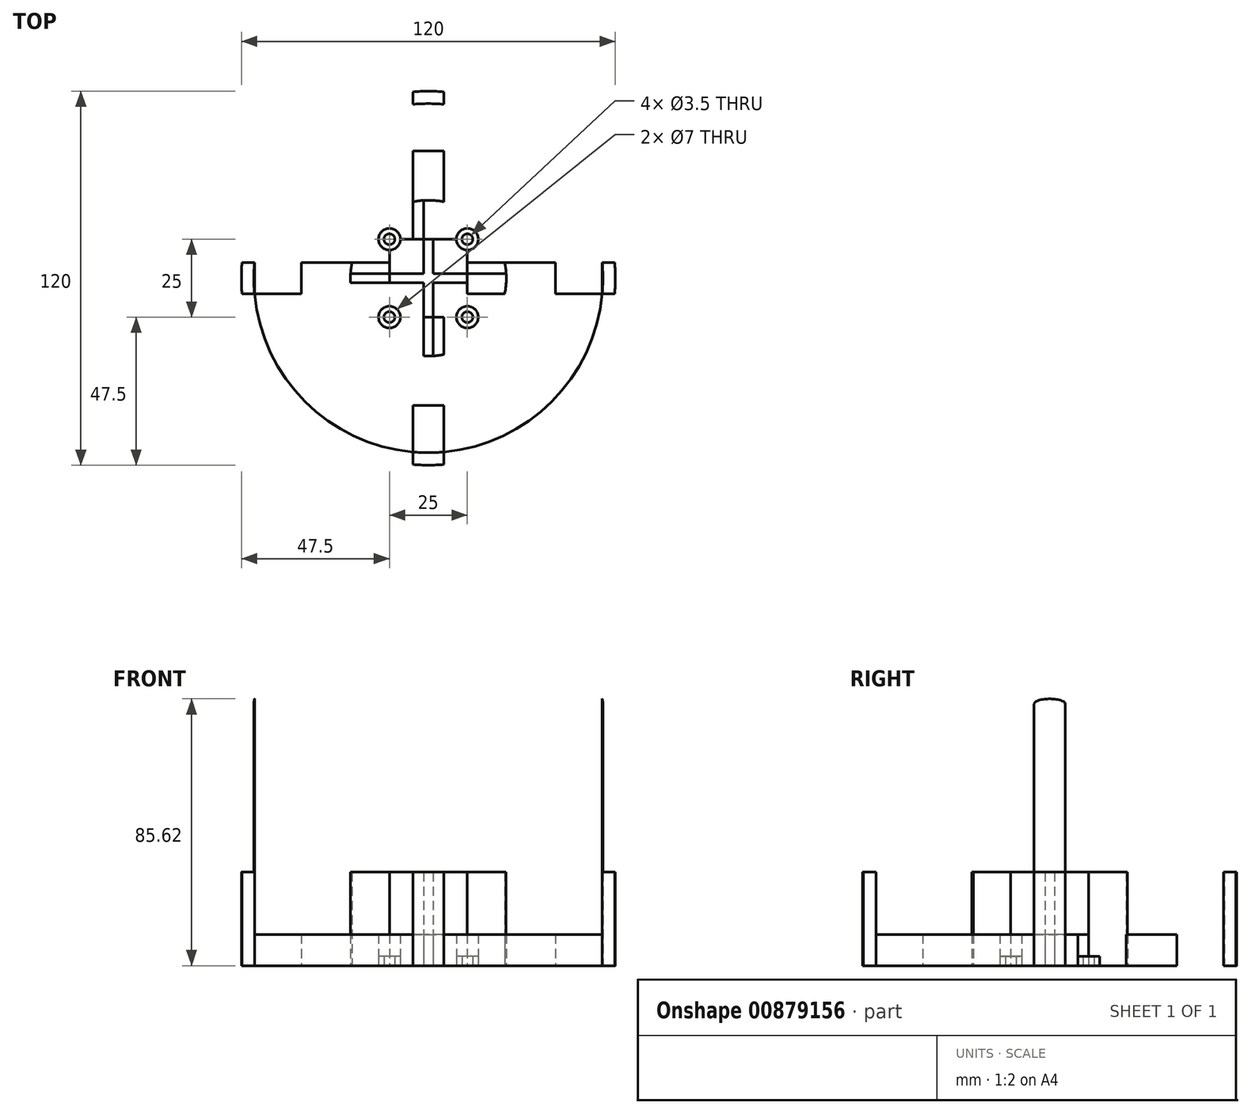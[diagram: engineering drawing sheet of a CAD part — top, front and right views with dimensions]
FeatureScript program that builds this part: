
annotation { "Feature Type Name" : "Feature", "Feature Type Description" : "" }
export const myFeature = defineFeature(function(context is Context, id is Id, definition is map)
    precondition{}
    {
        {
            var Q0;
            Q0=qCreatedBy(makeId("Top.planeOp"),FACE);
            var sketch = newSketch(context, id + "F0", { "sketchPlane" : qUnion([Q0])});
            skCircle(sketch, "E0", {"center": v(0, 0) * mm, "radius": 60 * mm});
            skCircle(sketch, "E1", {"center": v(0, 0) * mm, "radius": 56 * mm});
            skLineSegment(sketch, "E2.bottom", {"start": v(5, 55.78) * mm, "end": v(-5, 55.78) * mm});
            skLineSegment(sketch, "E2.top", {"start": v(5, -55.78) * mm, "end": v(-5, -55.78) * mm});
            skLineSegment(sketch, "E2.left", {"start": v(5, 55.78) * mm, "end": v(5, -55.78) * mm});
            skLineSegment(sketch, "E2.right", {"start": v(-5, 55.78) * mm, "end": v(-5, -55.78) * mm});
            skLineSegment(sketch, "E3.bottom", {"start": v(55.78, -5) * mm, "end": v(-55.78, -5) * mm});
            skLineSegment(sketch, "E3.top", {"start": v(55.78, 5) * mm, "end": v(-55.78, 5) * mm});
            skLineSegment(sketch, "E3.left", {"start": v(55.78, -5) * mm, "end": v(55.78, 5) * mm});
            skLineSegment(sketch, "E3.right", {"start": v(-55.78, -5) * mm, "end": v(-55.78, 5) * mm});
            skLineSegment(sketch, "E4.bottom", {"start": v(-5, 55.78) * mm, "end": v(5, 55.78) * mm});
            skLineSegment(sketch, "E4.top", {"start": v(-5, 40.78) * mm, "end": v(5, 40.78) * mm});
            skLineSegment(sketch, "E4.left", {"start": v(-5, 55.78) * mm, "end": v(-5, 40.78) * mm});
            skLineSegment(sketch, "E4.right", {"start": v(5, 55.78) * mm, "end": v(5, 40.78) * mm});
            skLineSegment(sketch, "E5.bottom", {"start": v(-55.78, -5) * mm, "end": v(-40.78, -5) * mm});
            skLineSegment(sketch, "E5.top", {"start": v(-55.78, 5) * mm, "end": v(-40.78, 5) * mm});
            skLineSegment(sketch, "E5.right", {"start": v(-40.78, -5) * mm, "end": v(-40.78, 5) * mm});
            skLineSegment(sketch, "E6.bottom", {"start": v(-5, -55.78) * mm, "end": v(5, -55.78) * mm});
            skLineSegment(sketch, "E6.top", {"start": v(-5, -40.78) * mm, "end": v(5, -40.78) * mm});
            skLineSegment(sketch, "E6.left", {"start": v(-5, -55.78) * mm, "end": v(-5, -40.78) * mm});
            skLineSegment(sketch, "E6.right", {"start": v(5, -55.78) * mm, "end": v(5, -40.78) * mm});
            skLineSegment(sketch, "E7.bottom", {"start": v(55.78, -5) * mm, "end": v(40.78, -5) * mm});
            skLineSegment(sketch, "E7.top", {"start": v(55.78, 5) * mm, "end": v(40.78, 5) * mm});
            skLineSegment(sketch, "E7.right", {"start": v(40.78, -5) * mm, "end": v(40.78, 5) * mm});
            skCircle(sketch, "E8", {"center": v(0, 0) * mm, "radius": 25 * mm});
            skLineSegment(sketch, "E9", {"start": v(-55.78, 5) * mm, "end": v(-59.8, 5) * mm});
            skLineSegment(sketch, "E10", {"start": v(-55.78, -5) * mm, "end": v(-59.8, -5) * mm});
            skLineSegment(sketch, "E11", {"start": v(-5, 55.78) * mm, "end": v(-5, 59.8) * mm});
            skLineSegment(sketch, "E12", {"start": v(5, 55.78) * mm, "end": v(5, 59.8) * mm});
            skLineSegment(sketch, "E13", {"start": v(55.78, 5) * mm, "end": v(59.8, 5) * mm});
            skLineSegment(sketch, "E14", {"start": v(55.78, -5) * mm, "end": v(59.8, -5) * mm});
            skLineSegment(sketch, "E15", {"start": v(-5, -55.78) * mm, "end": v(-5, -59.8) * mm});
            skLineSegment(sketch, "E16", {"start": v(5, -55.78) * mm, "end": v(5, -59.8) * mm});
            skLineSegment(sketch, "E17.bottom", {"start": v(12.5, 12.5) * mm, "end": v(-12.5, 12.5) * mm});
            skLineSegment(sketch, "E17.top", {"start": v(12.5, -12.5) * mm, "end": v(-12.5, -12.5) * mm});
            skLineSegment(sketch, "E17.left", {"start": v(12.5, 12.5) * mm, "end": v(12.5, -12.5) * mm});
            skLineSegment(sketch, "E17.right", {"start": v(-12.5, 12.5) * mm, "end": v(-12.5, -12.5) * mm});
            skCircle(sketch, "E18", {"center": v(-12.5, 12.5) * mm, "radius": 3.5 * mm});
            skCircle(sketch, "E19", {"center": v(-12.5, 12.5) * mm, "radius": 1.75 * mm});
            skCircle(sketch, "E20", {"center": v(12.5, 12.5) * mm, "radius": 3.5 * mm});
            skCircle(sketch, "E21", {"center": v(12.5, 12.5) * mm, "radius": 1.75 * mm});
            skCircle(sketch, "E22", {"center": v(-12.5, -12.5) * mm, "radius": 3.5 * mm});
            skCircle(sketch, "E23", {"center": v(-12.5, -12.5) * mm, "radius": 1.75 * mm});
            skCircle(sketch, "E24", {"center": v(12.5, -12.5) * mm, "radius": 3.5 * mm});
            skCircle(sketch, "E25", {"center": v(12.5, -12.5) * mm, "radius": 1.75 * mm});
            skLineSegment(sketch, "E26.bottom", {"start": v(40.78, 1.5) * mm, "end": v(-40.78, 1.5) * mm});
            skLineSegment(sketch, "E26.top", {"start": v(40.78, -1.5) * mm, "end": v(-40.78, -1.5) * mm});
            skLineSegment(sketch, "E26.left", {"start": v(40.78, 1.5) * mm, "end": v(40.78, -1.5) * mm});
            skLineSegment(sketch, "E26.right", {"start": v(-40.78, 1.5) * mm, "end": v(-40.78, -1.5) * mm});
            skLineSegment(sketch, "E27.bottom", {"start": v(1.5, 40.78) * mm, "end": v(-1.5, 40.78) * mm});
            skLineSegment(sketch, "E27.top", {"start": v(1.5, -40.78) * mm, "end": v(-1.5, -40.78) * mm});
            skLineSegment(sketch, "E27.left", {"start": v(1.5, 40.78) * mm, "end": v(1.5, -40.78) * mm});
            skLineSegment(sketch, "E27.right", {"start": v(-1.5, 40.78) * mm, "end": v(-1.5, -40.78) * mm});
            skSolve(sketch);
        }
        {
            var Q0;
            {var subQ0=sQuery(id+"F0.wireOp",EDGE,"E8");var subQ1=sQuery(id+"F0.wireOp",EDGE,"E2.left");var subQ2=makeQuery(id+"F0.imprint","INTERSECT",VERTEX,{"disambiguationData":[OD(0.0)],"derivedFrom":[subQ1,subQ0]});Q0=makeQuery(id+"F0.imprint","IMPRINT",FACE,{"disambiguationData":[TD([[makeQuery(id+"F0.imprint","IMPRINT",EDGE,{"disambiguationData":[TD([[subQ2,-1.0]])],"derivedFrom":subQ1}),1.0]])]});}
            var Q1;
            {var subQ0=sQuery(id+"F0.wireOp",EDGE,"E8");var subQ1=sQuery(id+"F0.wireOp",EDGE,"E2.left");var subQ2=makeQuery(id+"F0.imprint","INTERSECT",VERTEX,{"disambiguationData":[OD(0.0)],"derivedFrom":[subQ1,subQ0]});Q1=makeQuery(id+"F0.imprint","IMPRINT",FACE,{"disambiguationData":[TD([[makeQuery(id+"F0.imprint","IMPRINT",EDGE,{"disambiguationData":[TD([[subQ2,-1.0]])],"derivedFrom":subQ1}),-1.0]])]});}
            var Q2;
            {var subQ1=sQuery(id+"F0.wireOp",EDGE,"E2.right");var subQ5=sQuery(id+"F0.wireOp",EDGE,"E8");var subQ6=makeQuery(id+"F0.imprint","INTERSECT",VERTEX,{"disambiguationData":[OD(0.0)],"derivedFrom":[subQ1,subQ5]});Q2=makeQuery(id+"F0.imprint","IMPRINT",FACE,{"disambiguationData":[TD([[makeQuery(id+"F0.imprint","IMPRINT",EDGE,{"disambiguationData":[TD([[subQ6,-1.0]])],"derivedFrom":subQ1}),-1.0]])]});}
            var Q3;
            {var subQ5=sQuery(id+"F0.wireOp",EDGE,"E2.right");var subQ7=sQuery(id+"F0.wireOp",EDGE,"E17.bottom");var subQ8=makeQuery(id+"F0.imprint","INTERSECT",VERTEX,{"derivedFrom":[subQ5,subQ7]});Q3=makeQuery(id+"F0.imprint","IMPRINT",FACE,{"disambiguationData":[TD([[makeQuery(id+"F0.imprint","IMPRINT",EDGE,{"disambiguationData":[TD([[subQ8,-1.0]])],"derivedFrom":subQ5}),-1.0]])]});}
            var Q4;
            {var subQ0=sQuery(id+"F0.wireOp",EDGE,"E17.bottom");var subQ1=sQuery(id+"F0.wireOp",EDGE,"E2.left");var subQ2=makeQuery(id+"F0.imprint","INTERSECT",VERTEX,{"derivedFrom":[subQ1,subQ0]});Q4=makeQuery(id+"F0.imprint","IMPRINT",FACE,{"disambiguationData":[TD([[makeQuery(id+"F0.imprint","IMPRINT",EDGE,{"disambiguationData":[TD([[subQ2,-1.0]])],"derivedFrom":subQ1}),-1.0]])]});}
            var Q5;
            {var subQ5=sQuery(id+"F0.wireOp",EDGE,"E2.left");var subQ7=sQuery(id+"F0.wireOp",EDGE,"E17.bottom");var subQ8=makeQuery(id+"F0.imprint","INTERSECT",VERTEX,{"derivedFrom":[subQ5,subQ7]});Q5=makeQuery(id+"F0.imprint","IMPRINT",FACE,{"disambiguationData":[TD([[makeQuery(id+"F0.imprint","IMPRINT",EDGE,{"disambiguationData":[TD([[subQ8,-1.0]])],"derivedFrom":subQ5}),1.0]])]});}
            var Q6;
            {var subQ0=sQuery(id+"F0.wireOp",EDGE,"E3.top");var subQ1=sQuery(id+"F0.wireOp",EDGE,"E2.left");var subQ2=makeQuery(id+"F0.imprint","INTERSECT",VERTEX,{"derivedFrom":[subQ1,subQ0]});Q6=makeQuery(id+"F0.imprint","IMPRINT",FACE,{"disambiguationData":[TD([[makeQuery(id+"F0.imprint","IMPRINT",EDGE,{"disambiguationData":[TD([[subQ2,-1.0]])],"derivedFrom":subQ1}),1.0]])]});}
            var Q7;
            {var subQ0=sQuery(id+"F0.wireOp",EDGE,"E3.top");var subQ1=sQuery(id+"F0.wireOp",EDGE,"E2.left");var subQ2=makeQuery(id+"F0.imprint","INTERSECT",VERTEX,{"derivedFrom":[subQ1,subQ0]});Q7=makeQuery(id+"F0.imprint","IMPRINT",FACE,{"disambiguationData":[TD([[makeQuery(id+"F0.imprint","IMPRINT",EDGE,{"disambiguationData":[TD([[subQ2,-1.0]])],"derivedFrom":subQ1}),-1.0]])]});}
            var Q8;
            {var subQ0=sQuery(id+"F0.wireOp",EDGE,"E3.top");var subQ1=sQuery(id+"F0.wireOp",EDGE,"E2.right");var subQ2=makeQuery(id+"F0.imprint","INTERSECT",VERTEX,{"derivedFrom":[subQ1,subQ0]});Q8=makeQuery(id+"F0.imprint","IMPRINT",FACE,{"disambiguationData":[TD([[makeQuery(id+"F0.imprint","IMPRINT",EDGE,{"disambiguationData":[TD([[subQ2,-1.0]])],"derivedFrom":subQ1}),-1.0]])]});}
            var Q9;
            {var subQ0=sQuery(id+"F0.wireOp",EDGE,"E17.right");var subQ1=sQuery(id+"F0.wireOp",EDGE,"E3.bottom");var subQ2=makeQuery(id+"F0.imprint","INTERSECT",VERTEX,{"derivedFrom":[subQ1,subQ0]});Q9=makeQuery(id+"F0.imprint","IMPRINT",FACE,{"disambiguationData":[TD([[makeQuery(id+"F0.imprint","IMPRINT",EDGE,{"disambiguationData":[TD([[subQ2,-1.0]])],"derivedFrom":subQ1}),-1.0]])]});}
            var Q10;
            {var subQ0=sQuery(id+"F0.wireOp",EDGE,"E17.top");var subQ1=sQuery(id+"F0.wireOp",EDGE,"E2.right");var subQ2=makeQuery(id+"F0.imprint","INTERSECT",VERTEX,{"derivedFrom":[subQ1,subQ0]});Q10=makeQuery(id+"F0.imprint","IMPRINT",FACE,{"disambiguationData":[TD([[makeQuery(id+"F0.imprint","IMPRINT",EDGE,{"disambiguationData":[TD([[subQ2,-1.0]])],"derivedFrom":subQ1}),-1.0]])]});}
            var Q11;
            {var subQ1=sQuery(id+"F0.wireOp",EDGE,"E3.bottom");var subQ7=sQuery(id+"F0.wireOp",EDGE,"E2.right");var subQ8=makeQuery(id+"F0.imprint","INTERSECT",VERTEX,{"derivedFrom":[subQ7,subQ1]});Q11=makeQuery(id+"F0.imprint","IMPRINT",FACE,{"disambiguationData":[TD([[makeQuery(id+"F0.imprint","IMPRINT",EDGE,{"disambiguationData":[TD([[subQ8,-1.0]])],"derivedFrom":subQ7}),-1.0]])]});}
            var Q12;
            {var subQ0=sQuery(id+"F0.wireOp",EDGE,"E3.bottom");var subQ1=sQuery(id+"F0.wireOp",EDGE,"E2.left");var subQ2=makeQuery(id+"F0.imprint","INTERSECT",VERTEX,{"derivedFrom":[subQ1,subQ0]});Q12=makeQuery(id+"F0.imprint","IMPRINT",FACE,{"disambiguationData":[TD([[makeQuery(id+"F0.imprint","IMPRINT",EDGE,{"disambiguationData":[TD([[subQ2,-1.0]])],"derivedFrom":subQ1}),-1.0]])]});}
            var Q13;
            {var subQ1=sQuery(id+"F0.wireOp",EDGE,"E3.bottom");var subQ7=sQuery(id+"F0.wireOp",EDGE,"E2.left");var subQ8=makeQuery(id+"F0.imprint","INTERSECT",VERTEX,{"derivedFrom":[subQ7,subQ1]});Q13=makeQuery(id+"F0.imprint","IMPRINT",FACE,{"disambiguationData":[TD([[makeQuery(id+"F0.imprint","IMPRINT",EDGE,{"disambiguationData":[TD([[subQ8,-1.0]])],"derivedFrom":subQ7}),1.0]])]});}
            var Q14;
            {var subQ0=sQuery(id+"F0.wireOp",EDGE,"E17.top");var subQ1=sQuery(id+"F0.wireOp",EDGE,"E2.left");var subQ2=makeQuery(id+"F0.imprint","INTERSECT",VERTEX,{"derivedFrom":[subQ1,subQ0]});Q14=makeQuery(id+"F0.imprint","IMPRINT",FACE,{"disambiguationData":[TD([[makeQuery(id+"F0.imprint","IMPRINT",EDGE,{"disambiguationData":[TD([[subQ2,-1.0]])],"derivedFrom":subQ1}),1.0]])]});}
            var Q15;
            {var subQ0=sQuery(id+"F0.wireOp",EDGE,"E8");var subQ1=sQuery(id+"F0.wireOp",EDGE,"E3.bottom");var subQ2=makeQuery(id+"F0.imprint","INTERSECT",VERTEX,{"disambiguationData":[OD(0.0)],"derivedFrom":[subQ1,subQ0]});Q15=makeQuery(id+"F0.imprint","IMPRINT",FACE,{"disambiguationData":[TD([[makeQuery(id+"F0.imprint","IMPRINT",EDGE,{"disambiguationData":[TD([[subQ2,-1.0]])],"derivedFrom":subQ1}),-1.0]])]});}
            var Q16;
            {var subQ0=sQuery(id+"F0.wireOp",EDGE,"E17.top");var subQ1=sQuery(id+"F0.wireOp",EDGE,"E2.left");var subQ2=makeQuery(id+"F0.imprint","INTERSECT",VERTEX,{"derivedFrom":[subQ1,subQ0]});Q16=makeQuery(id+"F0.imprint","IMPRINT",FACE,{"disambiguationData":[TD([[makeQuery(id+"F0.imprint","IMPRINT",EDGE,{"disambiguationData":[TD([[subQ2,-1.0]])],"derivedFrom":subQ1}),-1.0]])]});}
            var Q17;
            {var subQ0=sQuery(id+"F0.wireOp",EDGE,"E6.top");Q17=makeQuery(id+"F0.imprint","IMPRINT",FACE,{"disambiguationData":[TD([[makeQuery(id+"F0.imprint","IMPRINT",EDGE,{"derivedFrom":subQ0}),1.0]])]});}
            var Q18;
            {var subQ0=sQuery(id+"F0.wireOp",EDGE,"E5.right");Q18=makeQuery(id+"F0.imprint","IMPRINT",FACE,{"disambiguationData":[TD([[makeQuery(id+"F0.imprint","IMPRINT",EDGE,{"derivedFrom":subQ0}),-1.0]])]});}
            var Q19;
            {var subQ0=sQuery(id+"F0.wireOp",EDGE,"E4.top");Q19=makeQuery(id+"F0.imprint","IMPRINT",FACE,{"disambiguationData":[TD([[makeQuery(id+"F0.imprint","IMPRINT",EDGE,{"derivedFrom":subQ0}),-1.0]])]});}
            var Q20;
            {var subQ0=sQuery(id+"F0.wireOp",EDGE,"E7.right");Q20=makeQuery(id+"F0.imprint","IMPRINT",FACE,{"disambiguationData":[TD([[makeQuery(id+"F0.imprint","IMPRINT",EDGE,{"derivedFrom":subQ0}),1.0]])]});}
            var Q21;
            {var subQ0=sQuery(id+"F0.wireOp",EDGE,"E8");var subQ1=sQuery(id+"F0.wireOp",EDGE,"E2.right");var subQ2=makeQuery(id+"F0.imprint","INTERSECT",VERTEX,{"disambiguationData":[OD(0.0)],"derivedFrom":[subQ1,subQ0]});Q21=makeQuery(id+"F0.imprint","IMPRINT",FACE,{"disambiguationData":[TD([[makeQuery(id+"F0.imprint","IMPRINT",EDGE,{"disambiguationData":[TD([[subQ2,-1.0]])],"derivedFrom":subQ1}),1.0]])]});}
            var Q22;
            {var subQ0=sQuery(id+"F0.wireOp",EDGE,"E17.bottom");var subQ1=sQuery(id+"F0.wireOp",EDGE,"E2.right");var subQ2=makeQuery(id+"F0.imprint","INTERSECT",VERTEX,{"derivedFrom":[subQ1,subQ0]});Q22=makeQuery(id+"F0.imprint","IMPRINT",FACE,{"disambiguationData":[TD([[makeQuery(id+"F0.imprint","IMPRINT",EDGE,{"disambiguationData":[TD([[subQ2,-1.0]])],"derivedFrom":subQ1}),1.0]])]});}
            var Q23;
            {var subQ0=sQuery(id+"F0.wireOp",EDGE,"E3.top");var subQ1=sQuery(id+"F0.wireOp",EDGE,"E2.right");var subQ2=makeQuery(id+"F0.imprint","INTERSECT",VERTEX,{"derivedFrom":[subQ1,subQ0]});Q23=makeQuery(id+"F0.imprint","IMPRINT",FACE,{"disambiguationData":[TD([[makeQuery(id+"F0.imprint","IMPRINT",EDGE,{"disambiguationData":[TD([[subQ2,-1.0]])],"derivedFrom":subQ1}),1.0]])]});}
            var Q24;
            {var subQ0=sQuery(id+"F0.wireOp",EDGE,"E17.right");var subQ1=sQuery(id+"F0.wireOp",EDGE,"E3.top");var subQ2=makeQuery(id+"F0.imprint","INTERSECT",VERTEX,{"derivedFrom":[subQ1,subQ0]});Q24=makeQuery(id+"F0.imprint","IMPRINT",FACE,{"disambiguationData":[TD([[makeQuery(id+"F0.imprint","IMPRINT",EDGE,{"disambiguationData":[TD([[subQ2,-1.0]])],"derivedFrom":subQ1}),1.0]])]});}
            var Q25;
            {var subQ0=sQuery(id+"F0.wireOp",EDGE,"E3.bottom");var subQ1=sQuery(id+"F0.wireOp",EDGE,"E2.right");var subQ2=makeQuery(id+"F0.imprint","INTERSECT",VERTEX,{"derivedFrom":[subQ1,subQ0]});Q25=makeQuery(id+"F0.imprint","IMPRINT",FACE,{"disambiguationData":[TD([[makeQuery(id+"F0.imprint","IMPRINT",EDGE,{"disambiguationData":[TD([[subQ2,-1.0]])],"derivedFrom":subQ1}),1.0]])]});}
            var Q26;
            {var subQ0=sQuery(id+"F0.wireOp",EDGE,"E17.top");var subQ1=sQuery(id+"F0.wireOp",EDGE,"E2.right");var subQ2=makeQuery(id+"F0.imprint","INTERSECT",VERTEX,{"derivedFrom":[subQ1,subQ0]});Q26=makeQuery(id+"F0.imprint","IMPRINT",FACE,{"disambiguationData":[TD([[makeQuery(id+"F0.imprint","IMPRINT",EDGE,{"disambiguationData":[TD([[subQ2,-1.0]])],"derivedFrom":subQ1}),1.0]])]});}
            var Q27;
            {var subQ0=sQuery(id+"F0.wireOp",EDGE,"E26.top");var subQ1=sQuery(id+"F0.wireOp",EDGE,"E2.right");var subQ2=makeQuery(id+"F0.imprint","INTERSECT",VERTEX,{"derivedFrom":[subQ1,subQ0]});Q27=makeQuery(id+"F0.imprint","IMPRINT",FACE,{"disambiguationData":[TD([[makeQuery(id+"F0.imprint","IMPRINT",EDGE,{"disambiguationData":[TD([[subQ2,-1.0]])],"derivedFrom":subQ1}),-1.0]])]});}
            var Q28;
            {var subQ0=sQuery(id+"F0.wireOp",EDGE,"E26.top");var subQ1=sQuery(id+"F0.wireOp",EDGE,"E2.right");var subQ2=makeQuery(id+"F0.imprint","INTERSECT",VERTEX,{"derivedFrom":[subQ1,subQ0]});Q28=makeQuery(id+"F0.imprint","IMPRINT",FACE,{"disambiguationData":[TD([[makeQuery(id+"F0.imprint","IMPRINT",EDGE,{"disambiguationData":[TD([[subQ2,-1.0]])],"derivedFrom":subQ1}),1.0]])]});}
            var Q29;
            {var subQ0=sQuery(id+"F0.wireOp",EDGE,"E26.top");var subQ1=sQuery(id+"F0.wireOp",EDGE,"E2.left");var subQ2=makeQuery(id+"F0.imprint","INTERSECT",VERTEX,{"derivedFrom":[subQ1,subQ0]});Q29=makeQuery(id+"F0.imprint","IMPRINT",FACE,{"disambiguationData":[TD([[makeQuery(id+"F0.imprint","IMPRINT",EDGE,{"disambiguationData":[TD([[subQ2,-1.0]])],"derivedFrom":subQ1}),-1.0]])]});}
            var Q30;
            {var subQ0=sQuery(id+"F0.wireOp",EDGE,"E26.top");var subQ1=sQuery(id+"F0.wireOp",EDGE,"E2.left");var subQ2=makeQuery(id+"F0.imprint","INTERSECT",VERTEX,{"derivedFrom":[subQ1,subQ0]});Q30=makeQuery(id+"F0.imprint","IMPRINT",FACE,{"disambiguationData":[TD([[makeQuery(id+"F0.imprint","IMPRINT",EDGE,{"disambiguationData":[TD([[subQ2,-1.0]])],"derivedFrom":subQ1}),1.0]])]});}
            var Q31;
            {var subQ0=sQuery(id+"F0.wireOp",EDGE,"E8");var subQ1=sQuery(id+"F0.wireOp",EDGE,"E3.top");var subQ2=makeQuery(id+"F0.imprint","INTERSECT",VERTEX,{"disambiguationData":[OD(0.0)],"derivedFrom":[subQ1,subQ0]});Q31=makeQuery(id+"F0.imprint","IMPRINT",FACE,{"disambiguationData":[TD([[makeQuery(id+"F0.imprint","IMPRINT",EDGE,{"disambiguationData":[TD([[subQ2,-1.0]])],"derivedFrom":subQ1}),1.0]])]});}
            extrude(context, id + "F1", {"entities" : qUnion([Q0, Q1, Q2, Q3, Q4, Q5, Q6, Q7, Q8, Q9, Q10, Q11, Q12, Q13, Q14, Q15, Q16, Q17, Q18, Q19, Q20, Q21, Q22, Q23, Q24, Q25, Q26, Q27, Q28, Q29, Q30, Q31]), "depth" : 10 * mm, "offsetDistance" : 25 * mm});
        }
        {
            var Q0;
            {var subQ5=sQuery(id+"F0.wireOp",EDGE,"E27.bottom");Q0=makeQuery(id+"F0.imprint","IMPRINT",FACE,{"disambiguationData":[TD([[makeQuery(id+"F0.imprint","IMPRINT",EDGE,{"derivedFrom":subQ5}),1.0]])]});}
            var Q1;
            {var subQ0=sQuery(id+"F0.wireOp",EDGE,"E27.left");var subQ1=sQuery(id+"F0.wireOp",EDGE,"E8");var subQ2=makeQuery(id+"F0.imprint","INTERSECT",VERTEX,{"disambiguationData":[OD(0.0)],"derivedFrom":[subQ1,subQ0]});Q1=makeQuery(id+"F0.imprint","IMPRINT",FACE,{"disambiguationData":[TD([[makeQuery(id+"F0.imprint","IMPRINT",EDGE,{"disambiguationData":[TD([[subQ2,-1.0]])],"derivedFrom":subQ1}),1.0]])]});}
            var Q2;
            {var subQ0=sQuery(id+"F0.wireOp",EDGE,"E27.left");var subQ1=sQuery(id+"F0.wireOp",EDGE,"E3.top");var subQ2=makeQuery(id+"F0.imprint","INTERSECT",VERTEX,{"derivedFrom":[subQ1,subQ0]});Q2=makeQuery(id+"F0.imprint","IMPRINT",FACE,{"disambiguationData":[TD([[makeQuery(id+"F0.imprint","IMPRINT",EDGE,{"disambiguationData":[TD([[subQ2,-1.0]])],"derivedFrom":subQ1}),-1.0]])]});}
            var Q3;
            {var subQ0=sQuery(id+"F0.wireOp",EDGE,"E27.left");var subQ1=sQuery(id+"F0.wireOp",EDGE,"E3.top");var subQ2=makeQuery(id+"F0.imprint","INTERSECT",VERTEX,{"derivedFrom":[subQ1,subQ0]});Q3=makeQuery(id+"F0.imprint","IMPRINT",FACE,{"disambiguationData":[TD([[makeQuery(id+"F0.imprint","IMPRINT",EDGE,{"disambiguationData":[TD([[subQ2,-1.0]])],"derivedFrom":subQ1}),1.0]])]});}
            var Q4;
            {var subQ0=sQuery(id+"F0.wireOp",EDGE,"E27.left");var subQ1=sQuery(id+"F0.wireOp",EDGE,"E26.bottom");var subQ2=makeQuery(id+"F0.imprint","INTERSECT",VERTEX,{"derivedFrom":[subQ1,subQ0]});Q4=makeQuery(id+"F0.imprint","IMPRINT",FACE,{"disambiguationData":[TD([[makeQuery(id+"F0.imprint","IMPRINT",EDGE,{"disambiguationData":[TD([[subQ2,-1.0]])],"derivedFrom":subQ1}),1.0]])]});}
            var Q5;
            {var subQ0=sQuery(id+"F0.wireOp",EDGE,"E27.left");var subQ1=sQuery(id+"F0.wireOp",EDGE,"E3.bottom");var subQ2=makeQuery(id+"F0.imprint","INTERSECT",VERTEX,{"derivedFrom":[subQ1,subQ0]});Q5=makeQuery(id+"F0.imprint","IMPRINT",FACE,{"disambiguationData":[TD([[makeQuery(id+"F0.imprint","IMPRINT",EDGE,{"disambiguationData":[TD([[subQ2,-1.0]])],"derivedFrom":subQ1}),-1.0]])]});}
            var Q6;
            {var subQ0=sQuery(id+"F0.wireOp",EDGE,"E27.left");var subQ1=sQuery(id+"F0.wireOp",EDGE,"E3.bottom");var subQ2=makeQuery(id+"F0.imprint","INTERSECT",VERTEX,{"derivedFrom":[subQ1,subQ0]});Q6=makeQuery(id+"F0.imprint","IMPRINT",FACE,{"disambiguationData":[TD([[makeQuery(id+"F0.imprint","IMPRINT",EDGE,{"disambiguationData":[TD([[subQ2,-1.0]])],"derivedFrom":subQ1}),1.0]])]});}
            var Q7;
            {var subQ0=sQuery(id+"F0.wireOp",EDGE,"E27.right");var subQ1=sQuery(id+"F0.wireOp",EDGE,"E8");var subQ2=makeQuery(id+"F0.imprint","INTERSECT",VERTEX,{"disambiguationData":[OD(1.0)],"derivedFrom":[subQ1,subQ0]});Q7=makeQuery(id+"F0.imprint","IMPRINT",FACE,{"disambiguationData":[TD([[makeQuery(id+"F0.imprint","IMPRINT",EDGE,{"disambiguationData":[TD([[subQ2,-1.0]])],"derivedFrom":subQ1}),1.0]])]});}
            var Q8;
            {var subQ5=sQuery(id+"F0.wireOp",EDGE,"E27.top");Q8=makeQuery(id+"F0.imprint","IMPRINT",FACE,{"disambiguationData":[TD([[makeQuery(id+"F0.imprint","IMPRINT",EDGE,{"derivedFrom":subQ5}),-1.0]])]});}
            var Q9;
            {var subQ0=sQuery(id+"F0.wireOp",EDGE,"E26.bottom");var subQ1=sQuery(id+"F0.wireOp",EDGE,"E2.left");var subQ2=makeQuery(id+"F0.imprint","INTERSECT",VERTEX,{"derivedFrom":[subQ1,subQ0]});Q9=makeQuery(id+"F0.imprint","IMPRINT",FACE,{"disambiguationData":[TD([[makeQuery(id+"F0.imprint","IMPRINT",EDGE,{"disambiguationData":[TD([[subQ2,-1.0]])],"derivedFrom":subQ1}),1.0]])]});}
            var Q10;
            {var subQ0=sQuery(id+"F0.wireOp",EDGE,"E26.bottom");var subQ1=sQuery(id+"F0.wireOp",EDGE,"E8");var subQ2=makeQuery(id+"F0.imprint","INTERSECT",VERTEX,{"disambiguationData":[OD(0.0)],"derivedFrom":[subQ1,subQ0]});Q10=makeQuery(id+"F0.imprint","IMPRINT",FACE,{"disambiguationData":[TD([[makeQuery(id+"F0.imprint","IMPRINT",EDGE,{"disambiguationData":[TD([[subQ2,1.0]])],"derivedFrom":subQ1}),1.0]])]});}
            var Q11;
            {var subQ5=sQuery(id+"F0.wireOp",EDGE,"E26.left");Q11=makeQuery(id+"F0.imprint","IMPRINT",FACE,{"disambiguationData":[TD([[makeQuery(id+"F0.imprint","IMPRINT",EDGE,{"derivedFrom":subQ5}),-1.0]])]});}
            var Q12;
            {var subQ0=sQuery(id+"F0.wireOp",EDGE,"E26.bottom");var subQ1=sQuery(id+"F0.wireOp",EDGE,"E2.right");var subQ2=makeQuery(id+"F0.imprint","INTERSECT",VERTEX,{"derivedFrom":[subQ1,subQ0]});Q12=makeQuery(id+"F0.imprint","IMPRINT",FACE,{"disambiguationData":[TD([[makeQuery(id+"F0.imprint","IMPRINT",EDGE,{"disambiguationData":[TD([[subQ2,-1.0]])],"derivedFrom":subQ1}),1.0]])]});}
            var Q13;
            {var subQ0=sQuery(id+"F0.wireOp",EDGE,"E26.bottom");var subQ1=sQuery(id+"F0.wireOp",EDGE,"E2.right");var subQ2=makeQuery(id+"F0.imprint","INTERSECT",VERTEX,{"derivedFrom":[subQ1,subQ0]});Q13=makeQuery(id+"F0.imprint","IMPRINT",FACE,{"disambiguationData":[TD([[makeQuery(id+"F0.imprint","IMPRINT",EDGE,{"disambiguationData":[TD([[subQ2,-1.0]])],"derivedFrom":subQ1}),-1.0]])]});}
            var Q14;
            {var subQ0=sQuery(id+"F0.wireOp",EDGE,"E26.bottom");var subQ1=sQuery(id+"F0.wireOp",EDGE,"E8");var subQ2=makeQuery(id+"F0.imprint","INTERSECT",VERTEX,{"disambiguationData":[OD(1.0)],"derivedFrom":[subQ1,subQ0]});Q14=makeQuery(id+"F0.imprint","IMPRINT",FACE,{"disambiguationData":[TD([[makeQuery(id+"F0.imprint","IMPRINT",EDGE,{"disambiguationData":[TD([[subQ2,-1.0]])],"derivedFrom":subQ1}),1.0]])]});}
            var Q15;
            {var subQ5=sQuery(id+"F0.wireOp",EDGE,"E26.right");Q15=makeQuery(id+"F0.imprint","IMPRINT",FACE,{"disambiguationData":[TD([[makeQuery(id+"F0.imprint","IMPRINT",EDGE,{"derivedFrom":subQ5}),1.0]])]});}
            var Q16;
            {var subQ0=sQuery(id+"F0.wireOp",EDGE,"E26.bottom");var subQ1=sQuery(id+"F0.wireOp",EDGE,"E2.left");var subQ2=makeQuery(id+"F0.imprint","INTERSECT",VERTEX,{"derivedFrom":[subQ1,subQ0]});Q16=makeQuery(id+"F0.imprint","IMPRINT",FACE,{"disambiguationData":[TD([[makeQuery(id+"F0.imprint","IMPRINT",EDGE,{"disambiguationData":[TD([[subQ2,-1.0]])],"derivedFrom":subQ1}),-1.0]])]});}
            var Q17;
            {var subQ0=sQuery(id+"F0.wireOp",EDGE,"E9");Q17=makeQuery(id+"F0.imprint","IMPRINT",FACE,{"disambiguationData":[TD([[makeQuery(id+"F0.imprint","IMPRINT",EDGE,{"derivedFrom":subQ0}),1.0]])]});}
            var Q18;
            {var subQ0=sQuery(id+"F0.wireOp",EDGE,"E13");Q18=makeQuery(id+"F0.imprint","IMPRINT",FACE,{"disambiguationData":[TD([[makeQuery(id+"F0.imprint","IMPRINT",EDGE,{"derivedFrom":subQ0}),-1.0]])]});}
            var Q19;
            {var subQ0=sQuery(id+"F0.wireOp",EDGE,"E11");Q19=makeQuery(id+"F0.imprint","IMPRINT",FACE,{"disambiguationData":[TD([[makeQuery(id+"F0.imprint","IMPRINT",EDGE,{"derivedFrom":subQ0}),-1.0]])]});}
            var Q20;
            {var subQ0=sQuery(id+"F0.wireOp",EDGE,"E15");Q20=makeQuery(id+"F0.imprint","IMPRINT",FACE,{"disambiguationData":[TD([[makeQuery(id+"F0.imprint","IMPRINT",EDGE,{"derivedFrom":subQ0}),1.0]])]});}
            extrude(context, id + "F2", {"entities" : qUnion([Q0, Q1, Q2, Q3, Q4, Q5, Q6, Q7, Q8, Q9, Q10, Q11, Q12, Q13, Q14, Q15, Q16, Q17, Q18, Q19, Q20]), "depth" : 30 * mm, "offsetDistance" : 25 * mm});
        }
        {
            var Q0;
            Q0=makeQuery(id+"F0.imprint","IMPRINT",FACE,{"disambiguationData":[TD([[makeQuery(id+"F0.imprint","IMPRINT",EDGE,{"derivedFrom":sQuery(id+"F0.wireOp",EDGE,"E4.bottom")}),-1.0]])]});
            var Q1;
            {var subQ1=sQuery(id+"F0.wireOp",EDGE,"E5.bottom");Q1=makeQuery(id+"F0.imprint","IMPRINT",FACE,{"disambiguationData":[TD([[makeQuery(id+"F0.imprint","IMPRINT",EDGE,{"derivedFrom":subQ1}),1.0]])]});}
            var Q2;
            Q2=makeQuery(id+"F0.imprint","IMPRINT",FACE,{"disambiguationData":[TD([[makeQuery(id+"F0.imprint","IMPRINT",EDGE,{"derivedFrom":sQuery(id+"F0.wireOp",EDGE,"E6.bottom")}),1.0]])]});
            var Q3;
            {var subQ1=sQuery(id+"F0.wireOp",EDGE,"E7.bottom");Q3=makeQuery(id+"F0.imprint","IMPRINT",FACE,{"disambiguationData":[TD([[makeQuery(id+"F0.imprint","IMPRINT",EDGE,{"derivedFrom":subQ1}),-1.0]])]});}
            var Q4;
            {var subQ0=sQuery(id+"F0.wireOp",EDGE,"E4.bottom");Q4=makeQuery(id+"F0.imprint","IMPRINT",FACE,{"disambiguationData":[TD([[makeQuery(id+"F0.imprint","IMPRINT",EDGE,{"derivedFrom":subQ0}),1.0]])]});}
            var Q5;
            {var subQ0=sQuery(id+"F0.wireOp",EDGE,"E3.left");Q5=makeQuery(id+"F0.imprint","IMPRINT",FACE,{"disambiguationData":[TD([[makeQuery(id+"F0.imprint","IMPRINT",EDGE,{"derivedFrom":subQ0}),-1.0]])]});}
            var Q6;
            {var subQ0=sQuery(id+"F0.wireOp",EDGE,"E3.right");Q6=makeQuery(id+"F0.imprint","IMPRINT",FACE,{"disambiguationData":[TD([[makeQuery(id+"F0.imprint","IMPRINT",EDGE,{"derivedFrom":subQ0}),1.0]])]});}
            var Q7;
            {var subQ0=sQuery(id+"F0.wireOp",EDGE,"E6.bottom");Q7=makeQuery(id+"F0.imprint","IMPRINT",FACE,{"disambiguationData":[TD([[makeQuery(id+"F0.imprint","IMPRINT",EDGE,{"derivedFrom":subQ0}),-1.0]])]});}
            extrude(context, id + "F3", {"entities" : qUnion([Q0, Q1, Q2, Q3, Q4, Q5, Q6, Q7]), "depth" : 90 * mm, "offsetDistance" : 25 * mm});
        }
        {
            var Q0;
            {var subQ0=sQuery(id+"F0.wireOp",EDGE,"E6.bottom");var subQ1=sQuery(id+"F0.wireOp",EDGE,"E1");Q0=makeQuery(id+"F3.opExtrude","CAP_EDGE",EDGE,{"disambiguationData":[OSD([subQ1]),TDD([makeQuery(id+"F0.imprint","IMPRINT",EDGE,{"disambiguationData":[TD([[makeQuery(id+"F0.imprint","INTERSECT",VERTEX,{"derivedFrom":[subQ1,subQ0,sQuery(id+"F0.wireOp",EDGE,"E6.left"),sQuery(id+"F0.wireOp",EDGE,"E15")]}),-1.0]])],"derivedFrom":subQ1})])],"isStart":false});}
            var Q1;
            {var subQ0=sQuery(id+"F0.wireOp",EDGE,"E3.right");var subQ1=sQuery(id+"F0.wireOp",EDGE,"E1");Q1=makeQuery(id+"F3.opExtrude","CAP_EDGE",EDGE,{"disambiguationData":[OSD([subQ1]),TDD([makeQuery(id+"F0.imprint","IMPRINT",EDGE,{"disambiguationData":[TD([[makeQuery(id+"F0.imprint","INTERSECT",VERTEX,{"derivedFrom":[subQ1,sQuery(id+"F0.wireOp",EDGE,"E5.bottom"),subQ0,sQuery(id+"F0.wireOp",EDGE,"E10")]}),1.0]])],"derivedFrom":subQ1})])],"isStart":false});}
            var Q2;
            {var subQ0=sQuery(id+"F0.wireOp",EDGE,"E4.bottom");var subQ1=sQuery(id+"F0.wireOp",EDGE,"E1");Q2=makeQuery(id+"F3.opExtrude","CAP_EDGE",EDGE,{"disambiguationData":[OSD([subQ1]),TDD([makeQuery(id+"F0.imprint","IMPRINT",EDGE,{"disambiguationData":[TD([[makeQuery(id+"F0.imprint","INTERSECT",VERTEX,{"derivedFrom":[subQ1,subQ0,sQuery(id+"F0.wireOp",EDGE,"E4.left"),sQuery(id+"F0.wireOp",EDGE,"E11")]}),1.0]])],"derivedFrom":subQ1})])],"isStart":false});}
            var Q3;
            {var subQ0=sQuery(id+"F0.wireOp",EDGE,"E3.left");var subQ1=sQuery(id+"F0.wireOp",EDGE,"E1");Q3=makeQuery(id+"F3.opExtrude","CAP_EDGE",EDGE,{"disambiguationData":[OSD([subQ1]),TDD([makeQuery(id+"F0.imprint","IMPRINT",EDGE,{"disambiguationData":[TD([[makeQuery(id+"F0.imprint","INTERSECT",VERTEX,{"derivedFrom":[subQ1,sQuery(id+"F0.wireOp",EDGE,"E7.bottom"),subQ0,sQuery(id+"F0.wireOp",EDGE,"E14")]}),-1.0]])],"derivedFrom":subQ1})])],"isStart":false});}
            fillet(context, id + "F4", {"entities" : qUnion([Q0, Q1, Q2, Q3]), "radius" : 6 * mm, "tangentPropagation" : true, "allowEdgeOverflow" : false});
        }
        {
            var Q0;
            {var subQ0=sQuery(id+"F0.wireOp",EDGE,"E18");var subQ1=sQuery(id+"F0.wireOp",EDGE,"E17.bottom");var subQ2=makeQuery(id+"F0.imprint","INTERSECT",VERTEX,{"derivedFrom":[subQ1,subQ0]});Q0=makeQuery(id+"F0.imprint","IMPRINT",FACE,{"disambiguationData":[TD([[makeQuery(id+"F0.imprint","IMPRINT",EDGE,{"disambiguationData":[TD([[subQ2,-1.0]])],"derivedFrom":subQ1}),-1.0]])]});}
            var Q1;
            {var subQ0=sQuery(id+"F0.wireOp",EDGE,"E18");var subQ1=sQuery(id+"F0.wireOp",EDGE,"E17.bottom");var subQ2=makeQuery(id+"F0.imprint","INTERSECT",VERTEX,{"derivedFrom":[subQ1,subQ0]});Q1=makeQuery(id+"F0.imprint","IMPRINT",FACE,{"disambiguationData":[TD([[makeQuery(id+"F0.imprint","IMPRINT",EDGE,{"disambiguationData":[TD([[subQ2,-1.0]])],"derivedFrom":subQ1}),1.0]])]});}
            var Q2;
            {var subQ0=sQuery(id+"F0.wireOp",EDGE,"E21");var subQ1=sQuery(id+"F0.wireOp",EDGE,"E17.bottom");var subQ2=makeQuery(id+"F0.imprint","INTERSECT",VERTEX,{"derivedFrom":[subQ1,subQ0]});Q2=makeQuery(id+"F0.imprint","IMPRINT",FACE,{"disambiguationData":[TD([[makeQuery(id+"F0.imprint","IMPRINT",EDGE,{"disambiguationData":[TD([[subQ2,-1.0]])],"derivedFrom":subQ1}),-1.0]])]});}
            var Q3;
            {var subQ0=sQuery(id+"F0.wireOp",EDGE,"E21");var subQ1=sQuery(id+"F0.wireOp",EDGE,"E17.bottom");var subQ2=makeQuery(id+"F0.imprint","INTERSECT",VERTEX,{"derivedFrom":[subQ1,subQ0]});Q3=makeQuery(id+"F0.imprint","IMPRINT",FACE,{"disambiguationData":[TD([[makeQuery(id+"F0.imprint","IMPRINT",EDGE,{"disambiguationData":[TD([[subQ2,-1.0]])],"derivedFrom":subQ1}),1.0]])]});}
            var Q4;
            {var subQ0=sQuery(id+"F0.wireOp",EDGE,"E22");var subQ1=sQuery(id+"F0.wireOp",EDGE,"E17.top");var subQ2=makeQuery(id+"F0.imprint","INTERSECT",VERTEX,{"derivedFrom":[subQ1,subQ0]});Q4=makeQuery(id+"F0.imprint","IMPRINT",FACE,{"disambiguationData":[TD([[makeQuery(id+"F0.imprint","IMPRINT",EDGE,{"disambiguationData":[TD([[subQ2,-1.0]])],"derivedFrom":subQ1}),1.0]])]});}
            var Q5;
            {var subQ0=sQuery(id+"F0.wireOp",EDGE,"E22");var subQ1=sQuery(id+"F0.wireOp",EDGE,"E17.top");var subQ2=makeQuery(id+"F0.imprint","INTERSECT",VERTEX,{"derivedFrom":[subQ1,subQ0]});Q5=makeQuery(id+"F0.imprint","IMPRINT",FACE,{"disambiguationData":[TD([[makeQuery(id+"F0.imprint","IMPRINT",EDGE,{"disambiguationData":[TD([[subQ2,-1.0]])],"derivedFrom":subQ1}),-1.0]])]});}
            var Q6;
            {var subQ0=sQuery(id+"F0.wireOp",EDGE,"E25");var subQ1=sQuery(id+"F0.wireOp",EDGE,"E17.top");var subQ2=makeQuery(id+"F0.imprint","INTERSECT",VERTEX,{"derivedFrom":[subQ1,subQ0]});Q6=makeQuery(id+"F0.imprint","IMPRINT",FACE,{"disambiguationData":[TD([[makeQuery(id+"F0.imprint","IMPRINT",EDGE,{"disambiguationData":[TD([[subQ2,-1.0]])],"derivedFrom":subQ1}),1.0]])]});}
            var Q7;
            {var subQ0=sQuery(id+"F0.wireOp",EDGE,"E25");var subQ1=sQuery(id+"F0.wireOp",EDGE,"E17.top");var subQ2=makeQuery(id+"F0.imprint","INTERSECT",VERTEX,{"derivedFrom":[subQ1,subQ0]});Q7=makeQuery(id+"F0.imprint","IMPRINT",FACE,{"disambiguationData":[TD([[makeQuery(id+"F0.imprint","IMPRINT",EDGE,{"disambiguationData":[TD([[subQ2,-1.0]])],"derivedFrom":subQ1}),-1.0]])]});}
            extrude(context, id + "F5", {"entities" : qUnion([Q0, Q1, Q2, Q3, Q4, Q5, Q6, Q7]), "depth" : 3 * mm, "offsetDistance" : 25 * mm});
        }
    });
